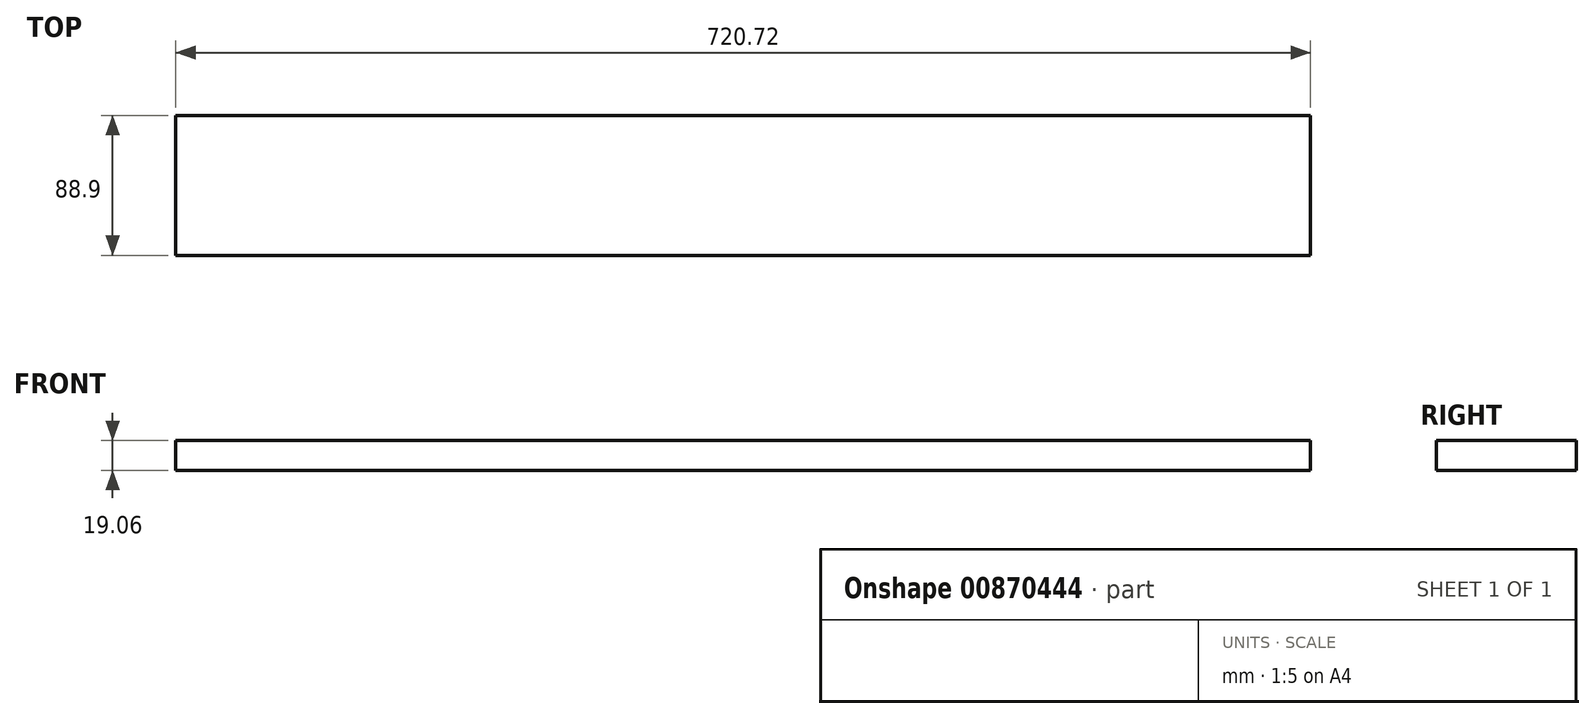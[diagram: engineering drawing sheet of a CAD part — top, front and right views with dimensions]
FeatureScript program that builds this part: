
annotation { "Feature Type Name" : "Feature", "Feature Type Description" : "" }
export const myFeature = defineFeature(function(context is Context, id is Id, definition is map)
    precondition{}
    {
        {
            var Q0;
            Q0=qCreatedBy(makeId("Right.planeOp"),FACE);
            var sketch = newSketch(context, id + "F0", { "sketchPlane" : qUnion([Q0])});
            skLineSegment(sketch, "E0.bottom", {"start": v(46.26, 9.53) * mm, "end": v(-42.64, 9.53) * mm});
            skLineSegment(sketch, "E0.top", {"start": v(46.26, -9.53) * mm, "end": v(-42.64, -9.53) * mm});
            skLineSegment(sketch, "E0.left", {"start": v(46.26, 9.53) * mm, "end": v(46.26, -9.52) * mm});
            skLineSegment(sketch, "E0.right", {"start": v(-42.64, 9.53) * mm, "end": v(-42.64, -9.52) * mm});
            skPoint(sketch, "E0.middle", {"position": v(1.8, 0) * mm});
            skSolve(sketch);
        }
        {
            var Q0;
            Q0=makeQuery(id+"F0.imprint","IMPRINT",FACE,{"disambiguationData":[TD([[makeQuery(id+"F0.imprint","IMPRINT",EDGE,{"derivedFrom":sQuery(id+"F0.wireOp",EDGE,"E0.bottom")}),1.0]])]});
            extrude(context, id + "F1", {"entities" : qUnion([Q0]), "depth" : 720.72 * mm, "offsetDistance" : 25.4 * mm});
        }
    });
